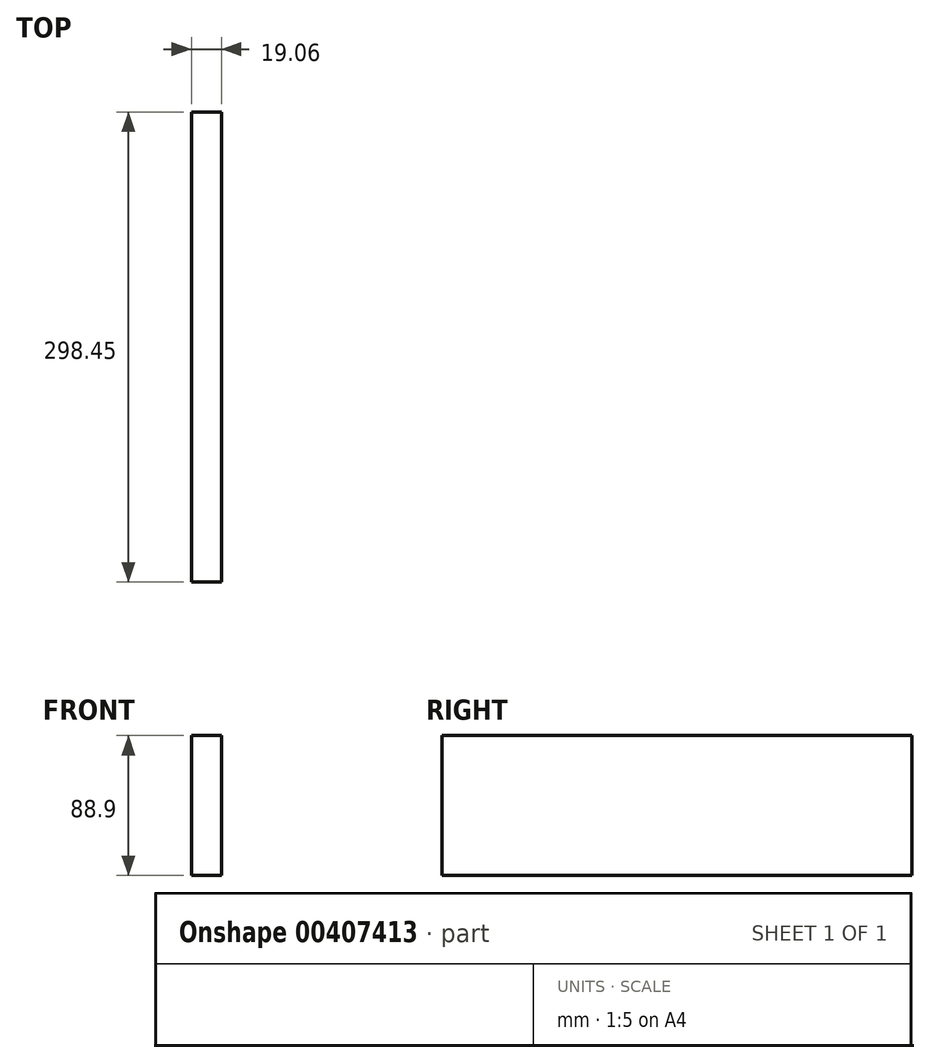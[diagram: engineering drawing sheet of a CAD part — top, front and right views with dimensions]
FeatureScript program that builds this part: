
annotation { "Feature Type Name" : "Feature", "Feature Type Description" : "" }
export const myFeature = defineFeature(function(context is Context, id is Id, definition is map)
    precondition{}
    {
        {
            var Q0;
            Q0=qCreatedBy(makeId("Front.planeOp"),FACE);
            var sketch = newSketch(context, id + "F0", { "sketchPlane" : qUnion([Q0])});
            skLineSegment(sketch, "E0.bottom", {"start": v(9.53, 44.45) * mm, "end": v(-9.52, 44.45) * mm});
            skLineSegment(sketch, "E0.top", {"start": v(9.52, -44.45) * mm, "end": v(-9.53, -44.45) * mm});
            skLineSegment(sketch, "E0.left", {"start": v(9.53, 44.45) * mm, "end": v(9.52, -44.45) * mm});
            skLineSegment(sketch, "E0.right", {"start": v(-9.52, 44.45) * mm, "end": v(-9.53, -44.45) * mm});
            skPoint(sketch, "E0.middle", {"position": v(0, 0) * mm});
            skSolve(sketch);
        }
        {
            var Q0;
            Q0=makeQuery(id+"F0.imprint","IMPRINT",FACE,{"disambiguationData":[TD([[makeQuery(id+"F0.imprint","IMPRINT",EDGE,{"derivedFrom":sQuery(id+"F0.wireOp",EDGE,"E0.bottom")}),1.0]])]});
            extrude(context, id + "F1", {"entities" : qUnion([Q0]), "depth" : 298.45 * mm});
        }
    });
